# Revit family: NBS_Allermuir_DmstcChrs-en-us-Tarry_LoungeChair
name_source: partatom
category: Furniture
revit_build: Autodesk Revit 2017 (Build: 20181011_1645(x64)
units: mm (PartAtom-declared; Revit-internal decimal feet)

## family parameters
Always vertical = Yes
Cut with Voids When Loaded = No
Room Calculation Point = No
Shared = No
Work Plane-Based = No

## types (2) — shared parameters
AssetType = Movable
Category = Pr_40_50_12_22:Dining chairs
CodePerformance = ANSI/BIFMA X5.1: 2017
DurationUnit = year
ExpectedLife = 10
IfcExportAs = IfcFurnitureType
IfcExportType = CHAIR
IsBuiltIn = No
ManufacturerName = Allermuir
ManufacturerURL = http://www.allermuir.com
NBSCertification = www.nationalbimlibrary.com/cert/05h2jfed
NBSDescription = Domestic chairs
NBSReference = 45-35-20/365
NominalDepth = 32 "
NominalLength = 29 "
NominalWidth = 29 "
OmniClassCode = 22-12 52 13
OmniClassTitle = Chairs
OmniClassVersion = Table 22 2012-05-16
ProductInformation = http://www.allermuir.com
SeatBaseMaterial = NBS_Concept
SeatFrameMaterial = NBS_Concept
SeatingSeatMaterial = NBS_Concept
SeatsAndBacksFinish = Upholstered
SeatsAndBacksMaterial = Upholstered
Size = 32 x 48.25 x 29.25 "
Status = UNSET
Style = Chair
Uniclass2015Code = Pr_40_50_12_22
Uniclass2015Title = Dining chairs
Uniclass2015Version = Products v1.12
Version = 2
WarrantyDescription = Allermuir warrant that its manufactured products are free from manufacturing defects - in materials or workmanship - for a period of five (5) years. , Allermuir will repair, or replace (at Allermuir's sole discretion) with comparable free of charge materials / components, any product / component which fails under normal use in a single shift environment, as a result of a defect in the materials and/ or workmanship
WarrantyDurationParts = 5
WarrantyDurationUnit = year
Weight = 73lbs
zero-valued in all types: HighestSeatingHeight, LowestSeatingHeight

## per-type parameters (varying)
| type | BIMObjectName | Description | Features | FramesFinish | FramesMaterial | Has4StarSwivelBase | HasWoodLegs | ModelReference | Name | NominalHeight | SeatingHeight |
| TAR405 | NBS_Allermuir_DomesticChairs_TarryLoungeChair_TAR405_US | Moulded foam construction with dual density back foam, height adjustable headrest, fully upholstered, solid ash legs with a clear finish, plastic glides, free floating seat tilt with upright locking,, optional feature: solid ash legs can be stained or colour washed , optional feature: plastic glides with felt, optional feature: two-tone upholstery | Swivel base | Black powder coat | Steel powder coated | Yes | No | TarryLoungeChair_TAR405 | DomesticChairs_TarryLoungeChair_TAR405_Allermuir | 49 " | 18 " |
| TAR403 | NBS_Allermuir_DomesticChairs_TarryLoungeChair_TAR403_US | Moulded foam construction with dual density back foam, height adjustable headrest, fully upholstered, solid ash legs with a clear finish, plastic glides,, optional feature: solid ash legs can be stained or colour washed , optional feature: plastic glides with felt, optional feature: two-tone upholstery | Wood legs | Clear | Solid ash | No | Yes | TarryLoungeChair_TAR403 | DomesticChairs_TarryLoungeChair_TAR403_Allermuir | 48 " | 17 " |

note: column(s) folded — value = type name in every type: ModelNumber

## geometry (parser evidence)
native form markers: Sweep x3
no freeform markers — native parametric forms only
